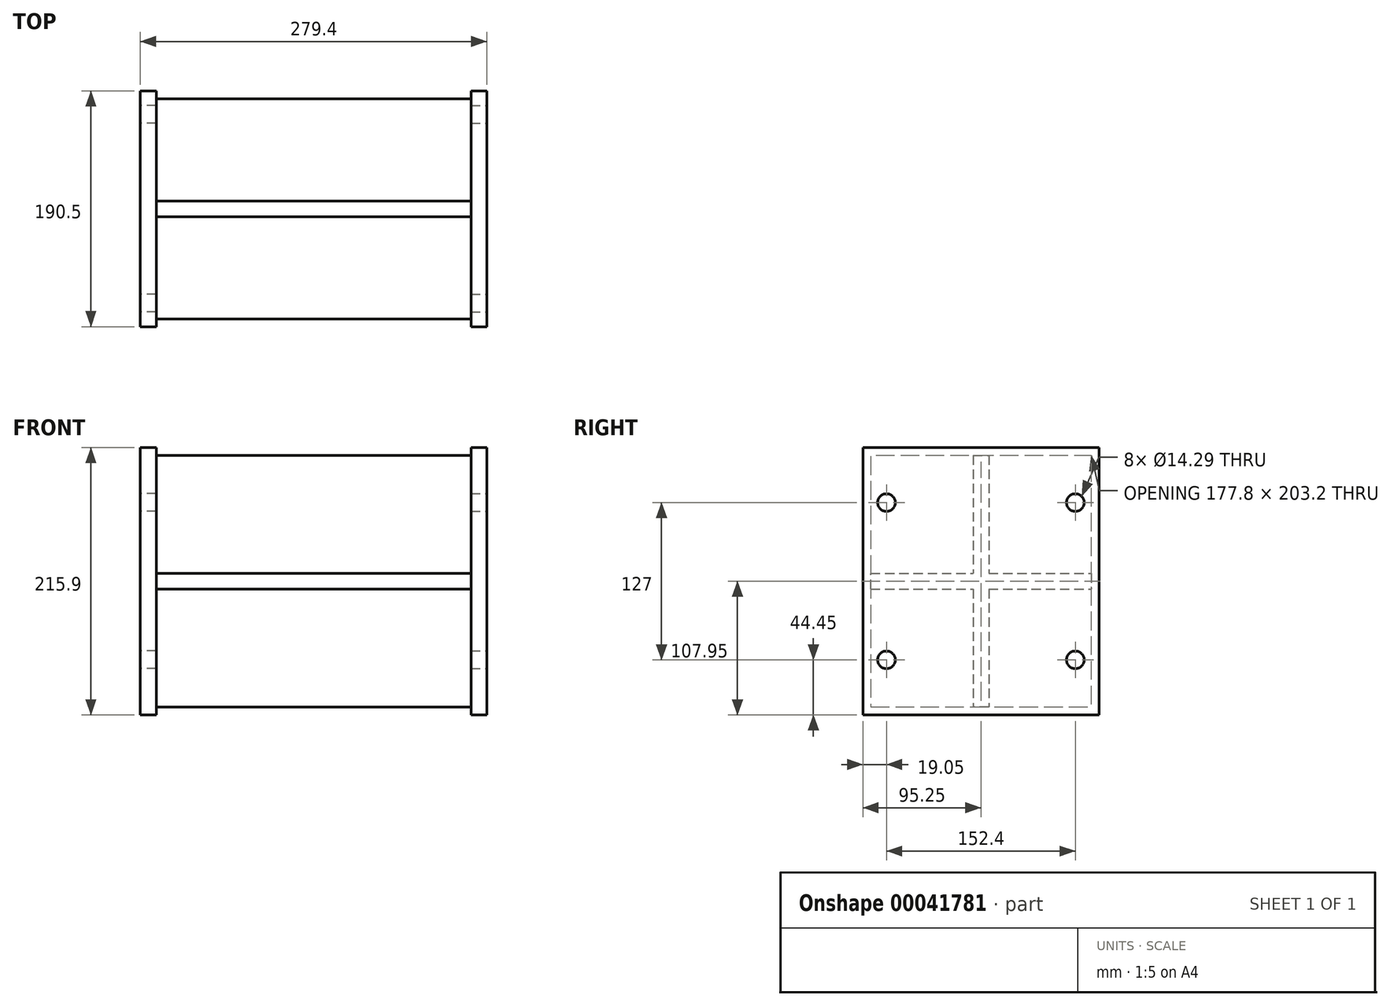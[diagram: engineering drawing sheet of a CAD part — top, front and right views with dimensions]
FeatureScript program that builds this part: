
annotation { "Feature Type Name" : "Feature", "Feature Type Description" : "" }
export const myFeature = defineFeature(function(context is Context, id is Id, definition is map)
    precondition{}
    {
        {
            var Q0;
            Q0=qCreatedBy(makeId("Right.planeOp"),FACE);
            var sketch = newSketch(context, id + "F0", { "sketchPlane" : qUnion([Q0])});
            skLineSegment(sketch, "E0.rect.bottom", {"start": v(-95.25, 107.95) * mm, "end": v(95.25, 107.95) * mm});
            skLineSegment(sketch, "E0.rect.top", {"start": v(-95.25, -107.95) * mm, "end": v(95.25, -107.95) * mm});
            skLineSegment(sketch, "E0.rect.left", {"start": v(-95.25, 107.95) * mm, "end": v(-95.25, -107.95) * mm});
            skLineSegment(sketch, "E0.rect.right", {"start": v(95.25, 107.95) * mm, "end": v(95.25, -107.95) * mm});
            skPoint(sketch, "E0.rect.middle", {"position": v(0, 0) * mm});
            skLineSegment(sketch, "E1", {"start": v(0, 107.95) * mm, "end": v(0, -107.95) * mm, "construction": true});
            skLineSegment(sketch, "E2.0", {"start": v(-95.25, 63.5) * mm, "end": v(95.25, 63.5) * mm, "construction": true});
            skLineSegment(sketch, "E3.0", {"start": v(-95.25, -63.5) * mm, "end": v(95.25, -63.5) * mm, "construction": true});
            skLineSegment(sketch, "E4.0", {"start": v(-76.2, 107.95) * mm, "end": v(-76.2, -107.95) * mm, "construction": true});
            skCircle(sketch, "E5", {"center": v(-76.2, 63.5) * mm, "radius": 7.14 * mm});
            skCircle(sketch, "E6", {"center": v(-76.2, -63.5) * mm, "radius": 7.14 * mm});
            skCircle(sketch, "E7.MirrorC", {"center": v(76.2, 63.5) * mm, "radius": 7.14 * mm});
            skCircle(sketch, "E8.MirrorC", {"center": v(76.2, -63.5) * mm, "radius": 7.14 * mm});
            skSolve(sketch);
        }
        {
            var Q0;
            Q0 = qSketchRegion(id + "F0", true);
            extrude(context, id + "F1", {"entities" : qUnion([Q0]), "depth" : 12.7 * mm});
        }
        {
            var Q0;
            Q0=qCreatedBy(makeId("Right.planeOp"),FACE);
            cPlane(context, id + "F2", {"entities" : qUnion([Q0]), "cplaneType" : CPlaneType.OFFSET, "offset" : 279.4 * mm, "width" : 152.4 * mm, "height" : 152.4 * mm});
        }
        {
            var Q0;
            Q0=qCreatedBy(id+"F2.planeOp",FACE);
            var sketch = newSketch(context, id + "F3", { "sketchPlane" : qUnion([Q0])});
            skCircle(sketch, "E9.0", {"center": v(76.2, 63.5) * mm, "radius": 7.14 * mm});
            skCircle(sketch, "E10.0", {"center": v(76.2, -63.5) * mm, "radius": 7.14 * mm});
            skCircle(sketch, "E11.0", {"center": v(-76.2, 63.5) * mm, "radius": 7.14 * mm});
            skLineSegment(sketch, "E12.0.0", {"start": v(95.25, 107.95) * mm, "end": v(-95.25, 107.95) * mm});
            skLineSegment(sketch, "E12.0.1", {"start": v(-95.25, 107.95) * mm, "end": v(-95.25, -107.95) * mm});
            skLineSegment(sketch, "E12.0.2", {"start": v(-95.25, -107.95) * mm, "end": v(95.25, -107.95) * mm});
            skLineSegment(sketch, "E12.0.3", {"start": v(95.25, -107.95) * mm, "end": v(95.25, 107.95) * mm});
            skCircle(sketch, "E13.0", {"center": v(-76.2, -63.5) * mm, "radius": 7.14 * mm});
            skSolve(sketch);
        }
        {
            var Q0;
            Q0 = qSketchRegion(id + "F3", true);
            extrude(context, id + "F4", {"entities" : qUnion([Q0]), "oppositeDirection" : true, "depth" : 12.7 * mm});
        }
        {
            var Q0;
            Q0=makeQuery(id+"F1.opExtrude","CAP_FACE",FACE,{"disambiguationData":[OSD([sQuery(id+"F0.wireOp",EDGE,"E0.rect.bottom"),sQuery(id+"F0.wireOp",EDGE,"E0.rect.top"),sQuery(id+"F0.wireOp",EDGE,"E0.rect.left"),sQuery(id+"F0.wireOp",EDGE,"E0.rect.right"),sQuery(id+"F0.wireOp",EDGE,"E5"),sQuery(id+"F0.wireOp",EDGE,"E6"),sQuery(id+"F0.wireOp",EDGE,"E7.MirrorC"),sQuery(id+"F0.wireOp",EDGE,"E8.MirrorC")])],"isStart":false});
            var sketch = newSketch(context, id + "F5", { "sketchPlane" : qUnion([Q0])});
            skLineSegment(sketch, "E14.0", {"start": v(-95.25, 101.6) * mm, "end": v(95.25, 101.6) * mm, "construction": true});
            skLineSegment(sketch, "E15.0", {"start": v(-95.25, -101.6) * mm, "end": v(95.25, -101.6) * mm, "construction": true});
            skLineSegment(sketch, "E16.0", {"start": v(-88.9, 107.95) * mm, "end": v(-88.9, -107.95) * mm, "construction": true});
            skLineSegment(sketch, "E17.0", {"start": v(88.9, 107.95) * mm, "end": v(88.9, -107.95) * mm, "construction": true});
            skLineSegment(sketch, "E18", {"start": v(0, 101.6) * mm, "end": v(0, -101.6) * mm, "construction": true});
            skLineSegment(sketch, "E19", {"start": v(-88.9, 0) * mm, "end": v(88.9, 0) * mm, "construction": true});
            skLineSegment(sketch, "E20.0", {"start": v(-6.35, 101.6) * mm, "end": v(-6.35, -101.6) * mm});
            skLineSegment(sketch, "E21.0", {"start": v(6.35, 101.6) * mm, "end": v(6.35, -101.6) * mm});
            skLineSegment(sketch, "E22.0", {"start": v(-88.9, -6.35) * mm, "end": v(88.9, -6.35) * mm});
            skLineSegment(sketch, "E23.0", {"start": v(-88.9, 6.35) * mm, "end": v(88.9, 6.35) * mm});
            skLineSegment(sketch, "E24", {"start": v(-6.35, 101.6) * mm, "end": v(6.35, 101.6) * mm});
            skLineSegment(sketch, "E25", {"start": v(88.9, 6.35) * mm, "end": v(88.9, -6.35) * mm});
            skLineSegment(sketch, "E26", {"start": v(6.35, -101.6) * mm, "end": v(-6.35, -101.6) * mm});
            skLineSegment(sketch, "E27", {"start": v(-88.9, -6.35) * mm, "end": v(-88.9, 6.35) * mm});
            skSolve(sketch);
        }
        {
            var Q0;
            Q0 = qSketchRegion(id + "F5", true);
            var Q1;
            Q1=makeQuery(id+"F4.opExtrude","CAP_FACE",FACE,{"disambiguationData":[OSD([sQuery(id+"F3.wireOp",EDGE,"E9.0"),sQuery(id+"F3.wireOp",EDGE,"E10.0"),sQuery(id+"F3.wireOp",EDGE,"E11.0"),sQuery(id+"F3.wireOp",EDGE,"E12.0.0"),sQuery(id+"F3.wireOp",EDGE,"E12.0.1"),sQuery(id+"F3.wireOp",EDGE,"E12.0.2"),sQuery(id+"F3.wireOp",EDGE,"E12.0.3"),sQuery(id+"F3.wireOp",EDGE,"E13.0")])],"isStart":false});
            extrude(context, id + "F6", {"entities" : qUnion([Q0]), "operationType" : NewBodyOperationType.ADD, "endBound" : BoundingType.UP_TO_SURFACE, "endBoundEntityFace" : qUnion([Q1]), "depth" : 25.4 * mm});
        }
    });
